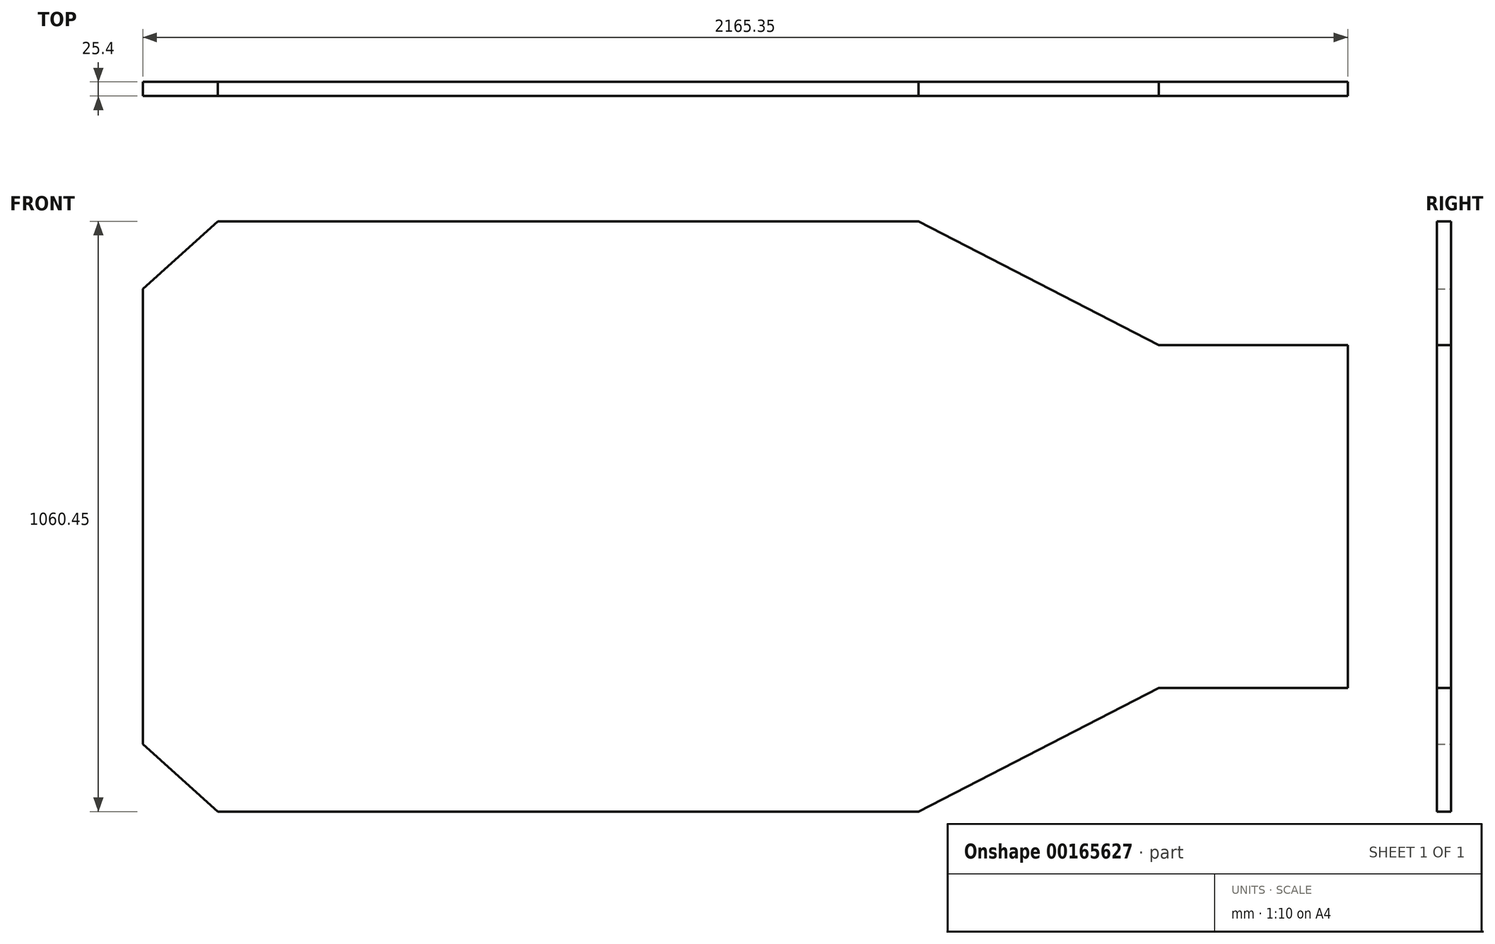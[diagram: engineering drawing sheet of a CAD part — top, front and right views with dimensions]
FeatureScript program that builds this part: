
annotation { "Feature Type Name" : "Feature", "Feature Type Description" : "" }
export const myFeature = defineFeature(function(context is Context, id is Id, definition is map)
    precondition{}
    {
        {
            var Q0;
            Q0=qCreatedBy(makeId("Front.planeOp"),FACE);
            var sketch = newSketch(context, id + "F0", { "sketchPlane" : qUnion([Q0])});
            skLineSegment(sketch, "E0.0", {"start": v(122.13, 933.45) * mm, "end": v(1381.03, 933.45) * mm});
            skLineSegment(sketch, "E0.1", {"start": v(-12.7, 812.1) * mm, "end": v(122.13, 933.45) * mm});
            skLineSegment(sketch, "E1.0", {"start": v(1812.83, 711.2) * mm, "end": v(2152.65, 711.2) * mm});
            skLineSegment(sketch, "E1.1", {"start": v(1381.03, 933.45) * mm, "end": v(1812.83, 711.2) * mm});
            skLineSegment(sketch, "E2.0", {"start": v(-12.7, -5.66) * mm, "end": v(-12.7, 812.1) * mm});
            skLineSegment(sketch, "E2.1", {"start": v(2152.65, 95.25) * mm, "end": v(1812.83, 95.25) * mm});
            skLineSegment(sketch, "E2.2", {"start": v(1381.03, -127) * mm, "end": v(1812.83, 95.25) * mm});
            skLineSegment(sketch, "E2.3", {"start": v(122.13, -127) * mm, "end": v(1381.03, -127) * mm});
            skLineSegment(sketch, "E2.4", {"start": v(-12.7, -5.66) * mm, "end": v(122.13, -127) * mm});
            skLineSegment(sketch, "E3.0", {"start": v(2152.65, 711.2) * mm, "end": v(2152.65, 95.25) * mm});
            skSolve(sketch);
        }
        {
            var Q0;
            Q0 = qSketchRegion(id + "F0", true);
            extrude(context, id + "F1", {"entities" : qUnion([Q0]), "depth" : 25.4 * mm});
        }
    });
